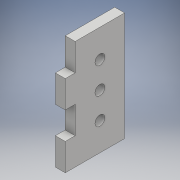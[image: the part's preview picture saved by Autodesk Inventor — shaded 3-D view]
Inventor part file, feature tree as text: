
AUTODESK INVENTOR PART (.ipt)
format: ipt  version: 2018 (Build 220112000, 112)  size: 111,616 bytes
history: native  units: mm
features: other x1, extrude x1, sketch x1
ambient origin geometry x8: Origin, YZ Plane, XZ Plane, XY Plane, X Axis, Y Axis, Z Axis, Center Point
bodies: Body1 (feature_tree)
feature tree (3):
  other  "Sólido1"
  extrude  "Extrusión1"  Depth=3.0mm
  sketch  "Boceto1"  dims[d0=33.0mm d4=3.0mm d5=3.0mm d6=3.0mm d8=8.25mm d9=8.25mm d10=8.25mm d11=8.25mm d12=3.0mm d13=0.0mm]
